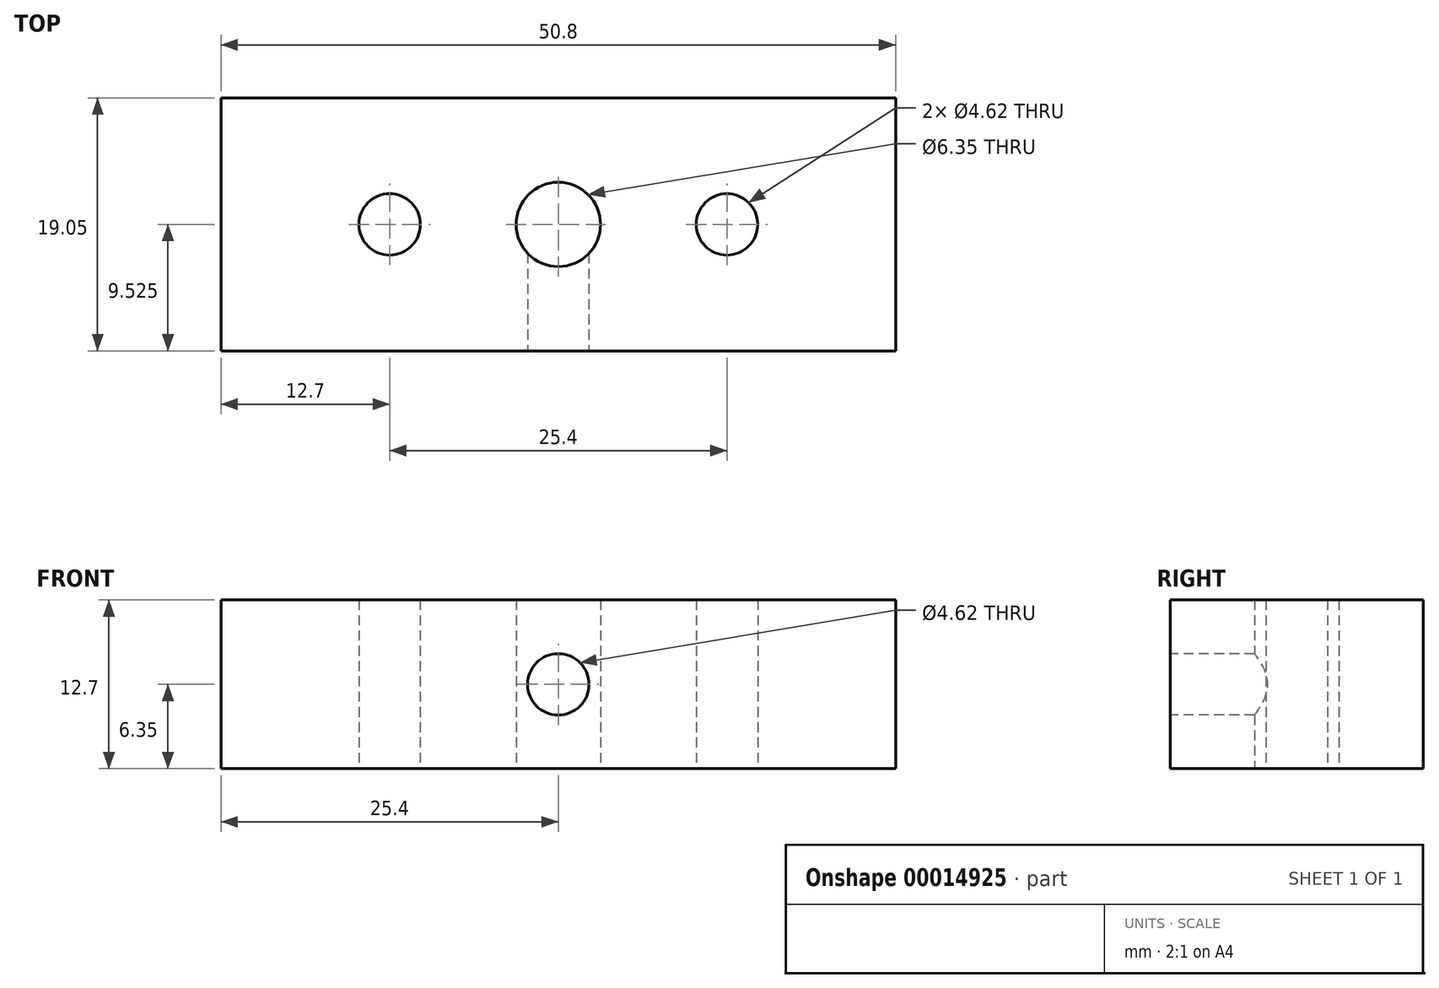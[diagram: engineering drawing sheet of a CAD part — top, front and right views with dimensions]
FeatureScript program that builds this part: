
annotation { "Feature Type Name" : "Feature", "Feature Type Description" : "" }
export const myFeature = defineFeature(function(context is Context, id is Id, definition is map)
    precondition{}
    {
        {
            var Q0;
            Q0=qCreatedBy(makeId("Top.planeOp"),FACE);
            var sketch = newSketch(context, id + "F0", { "sketchPlane" : qUnion([Q0])});
            skLineSegment(sketch, "E0.bottom", {"start": v(0, 0) * mm, "end": v(50.8, 0) * mm});
            skLineSegment(sketch, "E0.top", {"start": v(0, 19.05) * mm, "end": v(50.8, 19.05) * mm});
            skLineSegment(sketch, "E0.left", {"start": v(0, 0) * mm, "end": v(0, 19.05) * mm});
            skLineSegment(sketch, "E0.right", {"start": v(50.8, 0) * mm, "end": v(50.8, 19.05) * mm});
            skCircle(sketch, "E1", {"center": v(25.4, 9.53) * mm, "radius": 3.18 * mm});
            skCircle(sketch, "E2", {"center": v(12.7, 9.53) * mm, "radius": 2.31 * mm});
            skCircle(sketch, "E3", {"center": v(38.1, 9.53) * mm, "radius": 2.31 * mm});
            skSolve(sketch);
        }
        {
            var Q0;
            Q0=makeQuery(id+"F0.imprint","IMPRINT",FACE,{"disambiguationData":[TD([[makeQuery(id+"F0.imprint","IMPRINT",EDGE,{"derivedFrom":sQuery(id+"F0.wireOp",EDGE,"E0.bottom")}),1.0]])]});
            extrude(context, id + "F1", {"entities" : qUnion([Q0]), "depth" : 12.7 * mm});
        }
        {
            var Q0;
            Q0=makeQuery(id+"F1.opExtrude","SWEPT_FACE",FACE,{"disambiguationData":[OSD([sQuery(id+"F0.wireOp",EDGE,"E0.bottom")])]});
            var sketch = newSketch(context, id + "F2", { "sketchPlane" : qUnion([Q0])});
            skCircle(sketch, "E4", {"center": v(25.4, 6.35) * mm, "radius": 2.31 * mm});
            skSolve(sketch);
        }
        {
            var Q0;
            Q0=makeQuery(id+"F2.imprint","IMPRINT",FACE,{"disambiguationData":[TD([[makeQuery(id+"F2.imprint","IMPRINT",EDGE,{"derivedFrom":sQuery(id+"F2.wireOp",EDGE,"E4")}),1.0]])]});
            extrude(context, id + "F3", {"entities" : qUnion([Q0]), "operationType" : NewBodyOperationType.REMOVE, "oppositeDirection" : true, "depth" : 9.52 * mm});
        }
    });
